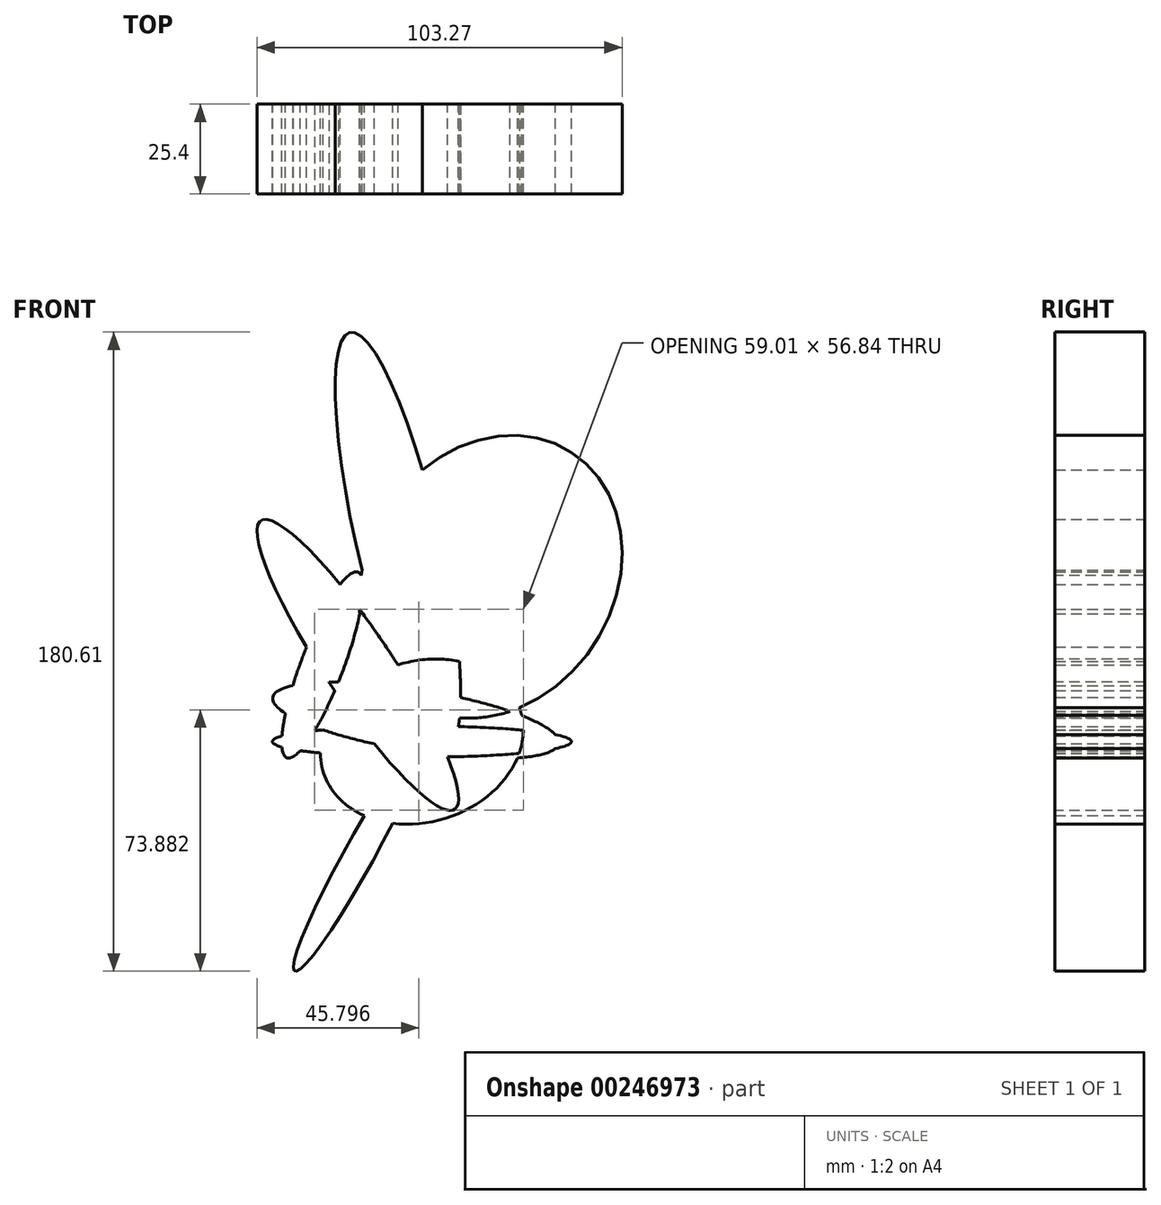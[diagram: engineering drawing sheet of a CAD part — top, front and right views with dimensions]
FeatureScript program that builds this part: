
annotation { "Feature Type Name" : "Feature", "Feature Type Description" : "" }
export const myFeature = defineFeature(function(context is Context, id is Id, definition is map)
    precondition{}
    {
        {
            var Q0;
            Q0=qCreatedBy(makeId("Front.planeOp"),FACE);
            var sketch = newSketch(context, id + "F0", { "sketchPlane" : qUnion([Q0])});
            skEllipse(sketch, "E0", {"center": v(6.78, -21.66) * mm, "majorRadius": 22.7 * mm, "minorRadius": 29.19 * mm, "majorAxis": v(-0.3, 0.95)});
            skEllipse(sketch, "E1", {"center": v(0, 35.07) * mm, "majorRadius": 60.47 * mm, "minorRadius": 11.76 * mm, "majorAxis": v(0.22, -0.97)});
            skEllipse(sketch, "E2", {"center": v(5.04, -15.65) * mm, "majorRadius": 40.96 * mm, "minorRadius": 8.72 * mm, "majorAxis": v(-0.99, 0.16)});
            skEllipse(sketch, "E3", {"center": v(-11.2, -54.07) * mm, "majorRadius": 37.06 * mm, "minorRadius": 4.2 * mm, "majorAxis": v(0.48, 0.87)});
            skEllipse(sketch, "E4", {"center": v(6.78, -21.66) * mm, "majorRadius": 42.28 * mm, "minorRadius": 4.39 * mm, "majorAxis": v(-1, 0)});
            skEllipse(sketch, "E5", {"center": v(-21.36, 0) * mm, "majorRadius": 28.07 * mm, "minorRadius": 6 * mm, "majorAxis": v(0.36, 0.93)});
            skEllipse(sketch, "E6", {"center": v(-11.34, 0) * mm, "majorRadius": 49.16 * mm, "minorRadius": 9.5 * mm, "majorAxis": v(0.56, -0.83)});
            skPoint(sketch, "E6.centerSnap0", {"position": v(-11.34, 26.23) * mm});
            skEllipse(sketch, "E7", {"center": v(26.23, 24.9) * mm, "majorRadius": 41.93 * mm, "minorRadius": 34.95 * mm, "majorAxis": v(-0.55, -0.84)});
            skSolve(sketch);
        }
        {
            var Q0;
            Q0 = qSketchRegion(id + "F0", true);
            extrude(context, id + "F1", {"entities" : qUnion([Q0]), "depth" : 25.4 * mm});
        }
    });
